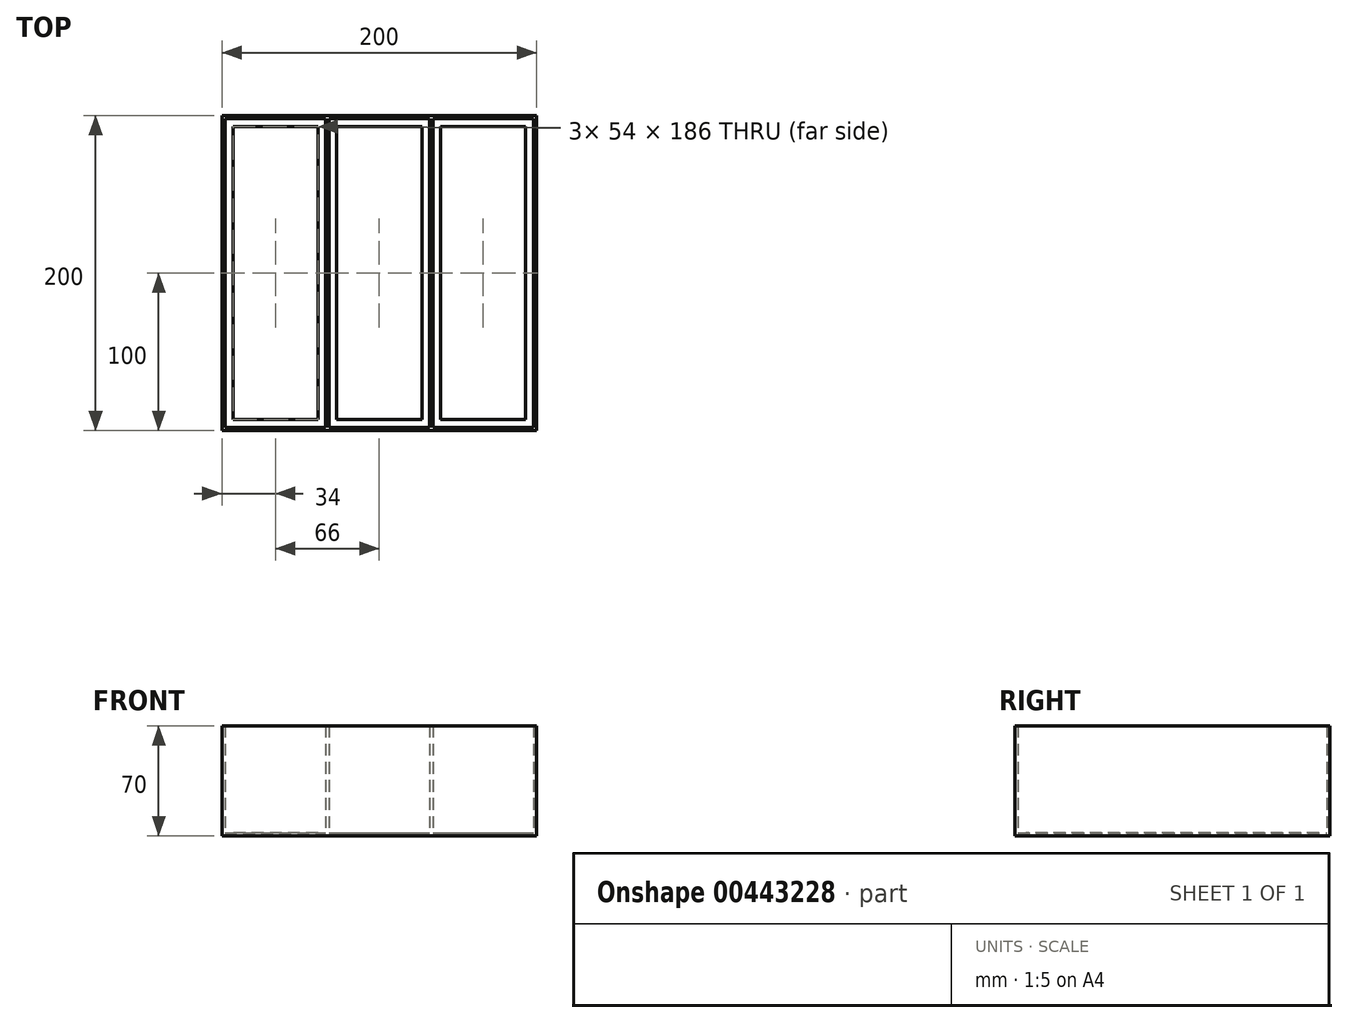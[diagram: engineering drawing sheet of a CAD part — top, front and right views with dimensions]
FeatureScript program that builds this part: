
annotation { "Feature Type Name" : "Feature", "Feature Type Description" : "" }
export const myFeature = defineFeature(function(context is Context, id is Id, definition is map)
    precondition{}
    {
        {
            var Q0;
            Q0=qCreatedBy(makeId("Top.planeOp"),FACE);
            var sketch = newSketch(context, id + "F0", { "sketchPlane" : qUnion([Q0])});
            skLineSegment(sketch, "E0.bottom", {"start": v(-100, 100) * mm, "end": v(100, 100) * mm});
            skLineSegment(sketch, "E0.top", {"start": v(-100, -100) * mm, "end": v(100, -100) * mm});
            skLineSegment(sketch, "E0.left", {"start": v(-100, 100) * mm, "end": v(-100, -100) * mm});
            skLineSegment(sketch, "E0.right", {"start": v(100, 100) * mm, "end": v(100, -100) * mm});
            skSolve(sketch);
        }
        {
            var Q0;
            Q0=makeQuery(id+"F0.imprint","IMPRINT",FACE,{"disambiguationData":[TD([[makeQuery(id+"F0.imprint","IMPRINT",EDGE,{"derivedFrom":sQuery(id+"F0.wireOp",EDGE,"E0.bottom")}),-1.0]])]});
            extrude(context, id + "F1", {"entities" : qUnion([Q0]), "depth" : 70 * mm, "offsetDistance" : 25 * mm});
        }
        {
            var Q0;
            Q0=makeQuery(id+"F1.opExtrude","CAP_FACE",FACE,{"disambiguationData":[OSD([sQuery(id+"F0.wireOp",EDGE,"E0.bottom"),sQuery(id+"F0.wireOp",EDGE,"E0.top"),sQuery(id+"F0.wireOp",EDGE,"E0.left"),sQuery(id+"F0.wireOp",EDGE,"E0.right")])],"isStart":false});
            shell(context, id + "F2", {"entities" : qUnion([Q0]), "thickness" : 2 * mm});
        }
        {
            var Q0;
            Q0=makeQuery(id+"F2.opShell","OFFSET_FACE",FACE,{"disambiguationData":[OSD([sQuery(id+"F0.wireOp",EDGE,"E0.bottom"),sQuery(id+"F0.wireOp",EDGE,"E0.top"),sQuery(id+"F0.wireOp",EDGE,"E0.left"),sQuery(id+"F0.wireOp",EDGE,"E0.right")])]});
            var sketch = newSketch(context, id + "F3", { "sketchPlane" : qUnion([Q0])});
            skLineSegment(sketch, "E1", {"start": v(-34, -98) * mm, "end": v(-34, 98) * mm});
            skLineSegment(sketch, "E2", {"start": v(32, -98) * mm, "end": v(32, 98) * mm});
            skLineSegment(sketch, "E3", {"start": v(-32, 98) * mm, "end": v(-32, -98) * mm});
            skLineSegment(sketch, "E4", {"start": v(34, 98) * mm, "end": v(34, -98) * mm});
            skSolve(sketch);
        }
        {
            var Q0;
            {var subQ0=sQuery(id+"F3.wireOp",EDGE,"E1");Q0=makeQuery(id+"F3.imprint","IMPRINT",FACE,{"disambiguationData":[TD([[makeQuery(id+"F3.imprint","IMPRINT",EDGE,{"derivedFrom":subQ0}),-1.0]])]});}
            var Q1;
            {var subQ0=sQuery(id+"F3.wireOp",EDGE,"E2");Q1=makeQuery(id+"F3.imprint","IMPRINT",FACE,{"disambiguationData":[TD([[makeQuery(id+"F3.imprint","IMPRINT",EDGE,{"derivedFrom":subQ0}),-1.0]])]});}
            extrude(context, id + "F4", {"entities" : qUnion([Q0, Q1]), "operationType" : NewBodyOperationType.ADD, "depth" : 68 * mm, "offsetDistance" : 25 * mm});
        }
        {
            var Q0;
            {var subQ0=sQuery(id+"F0.wireOp",EDGE,"E0.bottom");var subQ1=sQuery(id+"F0.wireOp",EDGE,"E0.top");var subQ2=sQuery(id+"F0.wireOp",EDGE,"E0.left");Q0=makeQuery(id+"F4.boolean.opBoolean","SPLIT",FACE,{"disambiguationData":[TD([makeQuery(id+"F2.opShell","OFFSET_FACE",FACE,{"disambiguationData":[OSD([subQ2])]})])],"derivedFrom":makeQuery(id+"F2.opShell","OFFSET_FACE",FACE,{"disambiguationData":[OSD([subQ0,subQ1,subQ2,sQuery(id+"F0.wireOp",EDGE,"E0.right")])]})});}
            var sketch = newSketch(context, id + "F5", { "sketchPlane" : qUnion([Q0])});
            skLineSegment(sketch, "E5.0.0", {"start": v(-98, -98) * mm, "end": v(-34, -98) * mm});
            skLineSegment(sketch, "E5.0.1", {"start": v(-34, -98) * mm, "end": v(-34, 98) * mm});
            skLineSegment(sketch, "E5.0.2", {"start": v(-34, 98) * mm, "end": v(-98, 98) * mm});
            skLineSegment(sketch, "E5.0.3", {"start": v(-98, 98) * mm, "end": v(-98, -98) * mm});
            skLineSegment(sketch, "E6.0.0", {"start": v(-32, -98) * mm, "end": v(32, -98) * mm});
            skLineSegment(sketch, "E6.0.1", {"start": v(32, -98) * mm, "end": v(32, 98) * mm});
            skLineSegment(sketch, "E6.0.2", {"start": v(32, 98) * mm, "end": v(-32, 98) * mm});
            skLineSegment(sketch, "E6.0.3", {"start": v(-32, 98) * mm, "end": v(-32, -98) * mm});
            skLineSegment(sketch, "E7.0.0", {"start": v(98, 98) * mm, "end": v(34, 98) * mm});
            skLineSegment(sketch, "E7.0.1", {"start": v(34, 98) * mm, "end": v(34, -98) * mm});
            skLineSegment(sketch, "E7.0.2", {"start": v(34, -98) * mm, "end": v(98, -98) * mm});
            skLineSegment(sketch, "E7.0.3", {"start": v(98, -98) * mm, "end": v(98, 98) * mm});
            skLineSegment(sketch, "E8.0", {"start": v(-93, 93) * mm, "end": v(-93, -93) * mm});
            skLineSegment(sketch, "E8.1", {"start": v(-39, 93) * mm, "end": v(-93, 93) * mm});
            skLineSegment(sketch, "E8.2", {"start": v(-39, -93) * mm, "end": v(-39, 93) * mm});
            skLineSegment(sketch, "E8.3", {"start": v(-93, -93) * mm, "end": v(-39, -93) * mm});
            skLineSegment(sketch, "E9.bottom", {"start": v(-93, 93) * mm, "end": v(-39, 93) * mm});
            skLineSegment(sketch, "E9.left", {"start": v(-93, 93) * mm, "end": v(-93, 53) * mm});
            skLineSegment(sketch, "E9.right", {"start": v(-39, 93) * mm, "end": v(-39, 53) * mm});
            skLineSegment(sketch, "E10.bottom", {"start": v(-93, 93) * mm, "end": v(-73, 93) * mm});
            skLineSegment(sketch, "E10.left", {"start": v(-93, 93) * mm, "end": v(-93, 70.53) * mm});
            skLineSegment(sketch, "E11.1.0.0", {"start": v(-27, 93) * mm, "end": v(27, 93) * mm});
            skLineSegment(sketch, "E11.1.0.1", {"start": v(27, -93) * mm, "end": v(27, 93) * mm});
            skLineSegment(sketch, "E11.1.0.2", {"start": v(-27, 93) * mm, "end": v(-27, -93) * mm});
            skLineSegment(sketch, "E11.1.0.3", {"start": v(-27, -93) * mm, "end": v(27, -93) * mm});
            skLineSegment(sketch, "E11.2.0.0", {"start": v(39, 93) * mm, "end": v(93, 93) * mm});
            skLineSegment(sketch, "E11.2.0.1", {"start": v(93, -93) * mm, "end": v(93, 93) * mm});
            skLineSegment(sketch, "E11.2.0.2", {"start": v(39, 93) * mm, "end": v(39, -93) * mm});
            skLineSegment(sketch, "E11.2.0.3", {"start": v(39, -93) * mm, "end": v(93, -93) * mm});
            skLineSegment(sketch, "E11.direction1", {"start": v(-93, 93) * mm, "end": v(-27, 93) * mm, "construction": true});
            skSolve(sketch);
        }
        {
            var Q0;
            Q0=makeQuery(id+"F5.imprint","IMPRINT",FACE,{"disambiguationData":[TD([[makeQuery(id+"F5.imprint","IMPRINT",EDGE,{"derivedFrom":sQuery(id+"F5.wireOp",EDGE,"E8.0")}),1.0]])]});
            var Q1;
            Q1=makeQuery(id+"F5.imprint","IMPRINT",FACE,{"disambiguationData":[TD([[makeQuery(id+"F5.imprint","IMPRINT",EDGE,{"derivedFrom":sQuery(id+"F5.wireOp",EDGE,"E11.1.0.0")}),-1.0]])]});
            var Q2;
            Q2=makeQuery(id+"F5.imprint","IMPRINT",FACE,{"disambiguationData":[TD([[makeQuery(id+"F5.imprint","IMPRINT",EDGE,{"derivedFrom":sQuery(id+"F5.wireOp",EDGE,"E11.2.0.0")}),-1.0]])]});
            extrude(context, id + "F6", {"entities" : qUnion([Q0, Q1, Q2]), "operationType" : NewBodyOperationType.REMOVE, "endBound" : BoundingType.UP_TO_NEXT, "oppositeDirection" : true, "depth" : 25 * mm, "offsetDistance" : 25 * mm});
        }
    });
